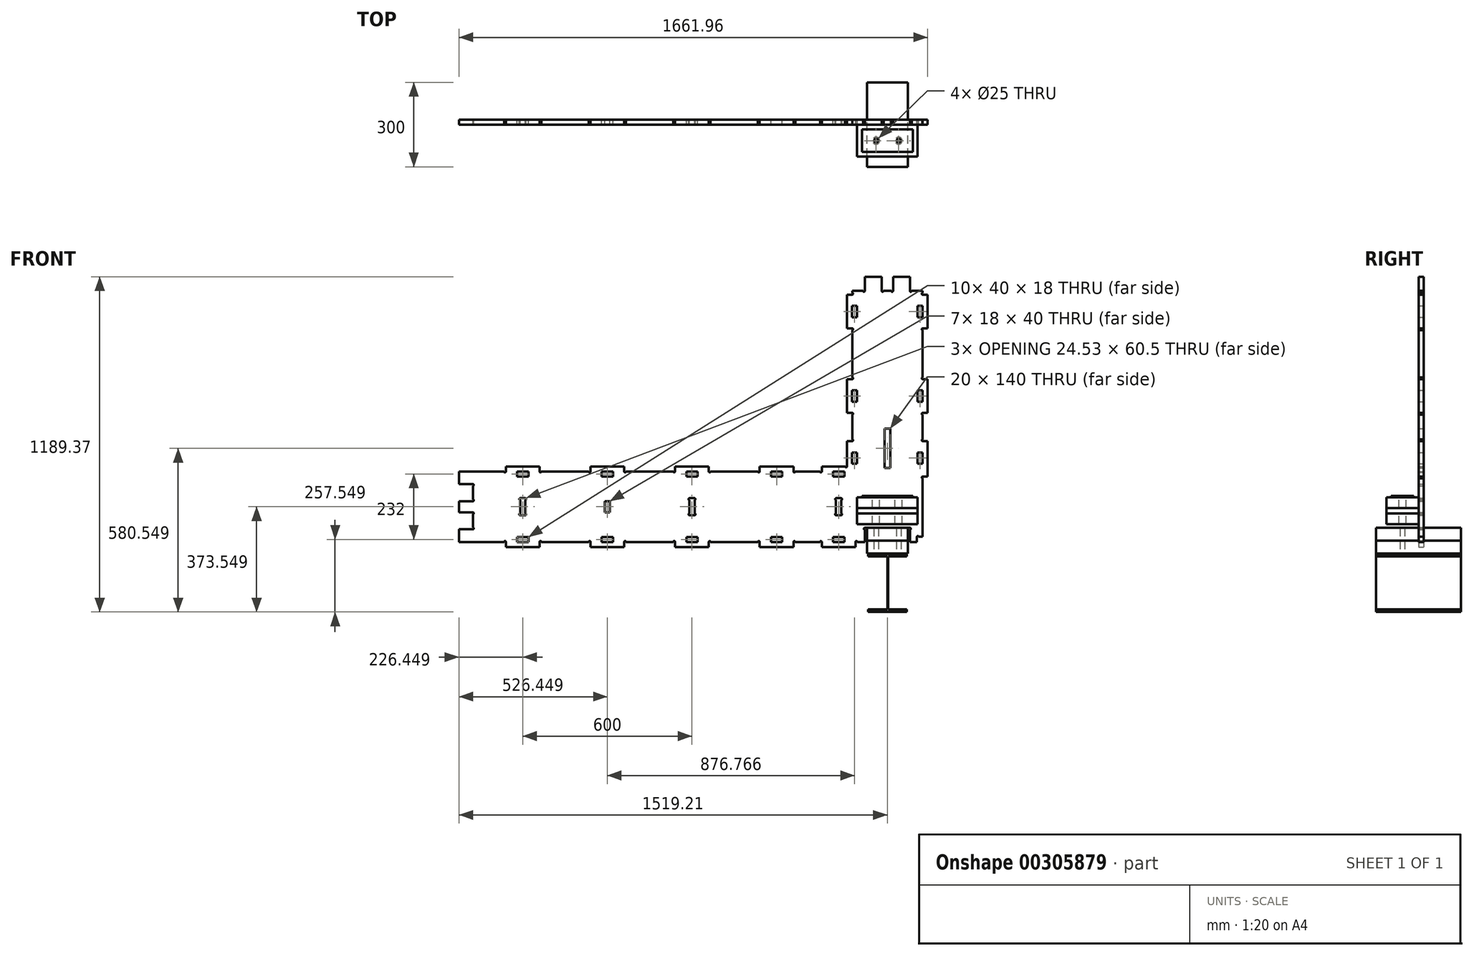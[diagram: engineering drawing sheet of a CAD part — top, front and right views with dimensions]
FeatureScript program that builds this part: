
annotation { "Feature Type Name" : "Feature", "Feature Type Description" : "" }
export const myFeature = defineFeature(function(context is Context, id is Id, definition is map)
    precondition{}
    {
        {
            var Q0;
            Q0=qCreatedBy(makeId("Front.planeOp"),FACE);
            var sketch = newSketch(context, id + "F0", { "sketchPlane" : qUnion([Q0])});
            skLineSegment(sketch, "E0", {"start": v(-425.29, 46.29) * mm, "end": v(-443.04, 46.29) * mm});
            skArc(sketch, "E1", {"start": v(-443.04, 46.29) * mm, "mid": v(-446.3, 49.43) * mm, "end": v(-443.29, 52.8) * mm});
            skLineSegment(sketch, "E2", {"start": v(-443.29, 52.8) * mm, "end": v(-443.29, 59.6) * mm});
            skLineSegment(sketch, "E3", {"start": v(-443.29, 59.6) * mm, "end": v(-481.77, 59.6) * mm});
            skArc(sketch, "E4", {"start": v(-481.77, 59.6) * mm, "mid": v(-485.15, 56.57) * mm, "end": v(-488.29, 59.84) * mm});
            skLineSegment(sketch, "E5", {"start": v(-488.29, 59.84) * mm, "end": v(-488.29, 109.6) * mm});
            skLineSegment(sketch, "E6", {"start": v(-488.29, 109.6) * mm, "end": v(-547.79, 109.6) * mm});
            skLineSegment(sketch, "E7", {"start": v(-547.79, 109.6) * mm, "end": v(-547.79, 59.84) * mm});
            skArc(sketch, "E8", {"start": v(-547.79, 59.84) * mm, "mid": v(-550.93, 56.58) * mm, "end": v(-554.3, 59.6) * mm});
            skLineSegment(sketch, "E9", {"start": v(-554.3, 59.6) * mm, "end": v(-581.77, 59.6) * mm});
            skArc(sketch, "E10", {"start": v(-581.77, 59.6) * mm, "mid": v(-585.15, 56.57) * mm, "end": v(-588.29, 59.84) * mm});
            skLineSegment(sketch, "E11", {"start": v(-588.29, 59.84) * mm, "end": v(-588.29, 109.6) * mm});
            skLineSegment(sketch, "E12", {"start": v(-588.29, 109.6) * mm, "end": v(-647.79, 109.6) * mm});
            skLineSegment(sketch, "E13", {"start": v(-647.79, 109.6) * mm, "end": v(-647.79, 59.84) * mm});
            skArc(sketch, "E14", {"start": v(-647.79, 59.84) * mm, "mid": v(-650.93, 56.58) * mm, "end": v(-654.3, 59.6) * mm});
            skLineSegment(sketch, "E15", {"start": v(-654.3, 59.6) * mm, "end": v(-692.79, 59.6) * mm});
            skLineSegment(sketch, "E16", {"start": v(-692.79, 59.6) * mm, "end": v(-692.79, 52.8) * mm});
            skArc(sketch, "E17", {"start": v(-692.79, 52.8) * mm, "mid": v(-689.77, 49.43) * mm, "end": v(-693.04, 46.29) * mm});
            skLineSegment(sketch, "E18", {"start": v(-693.04, 46.29) * mm, "end": v(-710.79, 46.29) * mm});
            skLineSegment(sketch, "E19", {"start": v(-710.79, 46.29) * mm, "end": v(-710.79, -73.21) * mm});
            skLineSegment(sketch, "E20", {"start": v(-710.79, -73.21) * mm, "end": v(-693.04, -73.21) * mm});
            skArc(sketch, "E21", {"start": v(-693.04, -73.21) * mm, "mid": v(-689.78, -76.35) * mm, "end": v(-692.79, -79.73) * mm});
            skLineSegment(sketch, "E22", {"start": v(-692.79, -79.73) * mm, "end": v(-692.79, -247.2) * mm});
            skArc(sketch, "E23", {"start": v(-692.79, -247.2) * mm, "mid": v(-689.77, -250.57) * mm, "end": v(-693.04, -253.71) * mm});
            skLineSegment(sketch, "E24", {"start": v(-693.04, -253.71) * mm, "end": v(-710.79, -253.71) * mm});
            skLineSegment(sketch, "E25", {"start": v(-710.79, -253.71) * mm, "end": v(-710.79, -373.21) * mm});
            skLineSegment(sketch, "E26", {"start": v(-710.79, -373.21) * mm, "end": v(-693.04, -373.21) * mm});
            skArc(sketch, "E27", {"start": v(-693.04, -373.21) * mm, "mid": v(-689.78, -376.35) * mm, "end": v(-692.79, -379.73) * mm});
            skLineSegment(sketch, "E28", {"start": v(-692.79, -379.73) * mm, "end": v(-692.79, -467.2) * mm});
            skArc(sketch, "E29", {"start": v(-692.79, -467.2) * mm, "mid": v(-689.77, -470.57) * mm, "end": v(-693.04, -473.71) * mm});
            skLineSegment(sketch, "E30", {"start": v(-693.04, -473.71) * mm, "end": v(-710.79, -473.71) * mm});
            skLineSegment(sketch, "E31", {"start": v(-710.79, -473.71) * mm, "end": v(-710.79, -563.23) * mm});
            skArc(sketch, "E32", {"start": v(-710.79, -563.23) * mm, "mid": v(-713.93, -566.49) * mm, "end": v(-717.3, -563.48) * mm});
            skLineSegment(sketch, "E33", {"start": v(-717.3, -563.48) * mm, "end": v(-800.55, -563.48) * mm});
            skLineSegment(sketch, "E34", {"start": v(-800.55, -563.48) * mm, "end": v(-800.55, -581.23) * mm});
            skArc(sketch, "E35", {"start": v(-800.55, -581.23) * mm, "mid": v(-803.7, -584.49) * mm, "end": v(-807.07, -581.48) * mm});
            skLineSegment(sketch, "E36", {"start": v(-807.07, -581.48) * mm, "end": v(-894.53, -581.48) * mm});
            skArc(sketch, "E37", {"start": v(-894.53, -581.48) * mm, "mid": v(-897.91, -584.5) * mm, "end": v(-901.05, -581.23) * mm});
            skLineSegment(sketch, "E38", {"start": v(-901.05, -581.23) * mm, "end": v(-901.05, -563.48) * mm});
            skLineSegment(sketch, "E39", {"start": v(-901.05, -563.48) * mm, "end": v(-1020.55, -563.48) * mm});
            skLineSegment(sketch, "E40", {"start": v(-1020.55, -563.48) * mm, "end": v(-1020.55, -581.23) * mm});
            skArc(sketch, "E41", {"start": v(-1020.55, -581.23) * mm, "mid": v(-1023.7, -584.49) * mm, "end": v(-1027.07, -581.48) * mm});
            skLineSegment(sketch, "E42", {"start": v(-1027.07, -581.48) * mm, "end": v(-1194.53, -581.48) * mm});
            skArc(sketch, "E43", {"start": v(-1194.53, -581.48) * mm, "mid": v(-1197.91, -584.5) * mm, "end": v(-1201.05, -581.23) * mm});
            skLineSegment(sketch, "E44", {"start": v(-1201.05, -581.23) * mm, "end": v(-1201.05, -563.48) * mm});
            skLineSegment(sketch, "E45", {"start": v(-1201.05, -563.48) * mm, "end": v(-1320.55, -563.48) * mm});
            skLineSegment(sketch, "E46", {"start": v(-1320.55, -563.48) * mm, "end": v(-1320.55, -581.23) * mm});
            skArc(sketch, "E47", {"start": v(-1320.55, -581.23) * mm, "mid": v(-1323.7, -584.49) * mm, "end": v(-1327.07, -581.48) * mm});
            skLineSegment(sketch, "E48", {"start": v(-1327.07, -581.48) * mm, "end": v(-1494.53, -581.48) * mm});
            skArc(sketch, "E49", {"start": v(-1494.53, -581.48) * mm, "mid": v(-1497.91, -584.5) * mm, "end": v(-1501.05, -581.23) * mm});
            skLineSegment(sketch, "E50", {"start": v(-1501.05, -581.23) * mm, "end": v(-1501.05, -563.48) * mm});
            skLineSegment(sketch, "E51", {"start": v(-1501.05, -563.48) * mm, "end": v(-1620.55, -563.48) * mm});
            skLineSegment(sketch, "E52", {"start": v(-1620.55, -563.48) * mm, "end": v(-1620.55, -581.23) * mm});
            skArc(sketch, "E53", {"start": v(-1620.55, -581.23) * mm, "mid": v(-1623.7, -584.49) * mm, "end": v(-1627.07, -581.48) * mm});
            skLineSegment(sketch, "E54", {"start": v(-1627.07, -581.48) * mm, "end": v(-1794.53, -581.48) * mm});
            skArc(sketch, "E55", {"start": v(-1794.53, -581.48) * mm, "mid": v(-1797.91, -584.5) * mm, "end": v(-1801.05, -581.23) * mm});
            skLineSegment(sketch, "E56", {"start": v(-1801.05, -581.23) * mm, "end": v(-1801.05, -563.48) * mm});
            skLineSegment(sketch, "E57", {"start": v(-1801.05, -563.48) * mm, "end": v(-1920.55, -563.48) * mm});
            skLineSegment(sketch, "E58", {"start": v(-1920.55, -563.48) * mm, "end": v(-1920.55, -581.23) * mm});
            skArc(sketch, "E59", {"start": v(-1920.55, -581.23) * mm, "mid": v(-1923.7, -584.49) * mm, "end": v(-1927.07, -581.48) * mm});
            skLineSegment(sketch, "E60", {"start": v(-1927.07, -581.48) * mm, "end": v(-2087.25, -581.48) * mm});
            skLineSegment(sketch, "E61", {"start": v(-2087.25, -581.48) * mm, "end": v(-2087.25, -625.98) * mm});
            skLineSegment(sketch, "E62", {"start": v(-2087.25, -625.98) * mm, "end": v(-2037.5, -625.98) * mm});
            skArc(sketch, "E63", {"start": v(-2037.5, -625.98) * mm, "mid": v(-2034.24, -629.12) * mm, "end": v(-2037.25, -632.5) * mm});
            skLineSegment(sketch, "E64", {"start": v(-2037.25, -632.5) * mm, "end": v(-2037.25, -679.96) * mm});
            skArc(sketch, "E65", {"start": v(-2037.25, -679.96) * mm, "mid": v(-2034.23, -683.34) * mm, "end": v(-2037.5, -686.48) * mm});
            skLineSegment(sketch, "E66", {"start": v(-2037.5, -686.48) * mm, "end": v(-2087.25, -686.48) * mm});
            skLineSegment(sketch, "E67", {"start": v(-2087.25, -686.48) * mm, "end": v(-2087.25, -725.98) * mm});
            skLineSegment(sketch, "E68", {"start": v(-2087.25, -725.98) * mm, "end": v(-2037.5, -725.98) * mm});
            skArc(sketch, "E69", {"start": v(-2037.5, -725.98) * mm, "mid": v(-2034.24, -729.12) * mm, "end": v(-2037.25, -732.5) * mm});
            skLineSegment(sketch, "E70", {"start": v(-2037.25, -732.5) * mm, "end": v(-2037.25, -779.96) * mm});
            skArc(sketch, "E71", {"start": v(-2037.25, -779.96) * mm, "mid": v(-2034.23, -783.34) * mm, "end": v(-2037.5, -786.48) * mm});
            skLineSegment(sketch, "E72", {"start": v(-2037.5, -786.48) * mm, "end": v(-2087.25, -786.48) * mm});
            skLineSegment(sketch, "E73", {"start": v(-2087.25, -786.48) * mm, "end": v(-2087.25, -830.98) * mm});
            skLineSegment(sketch, "E74", {"start": v(-2087.25, -830.98) * mm, "end": v(-1927.07, -830.98) * mm});
            skArc(sketch, "E75", {"start": v(-1927.07, -830.98) * mm, "mid": v(-1923.7, -827.96) * mm, "end": v(-1920.55, -831.23) * mm});
            skLineSegment(sketch, "E76", {"start": v(-1920.55, -831.23) * mm, "end": v(-1920.55, -848.98) * mm});
            skLineSegment(sketch, "E77", {"start": v(-1920.55, -848.98) * mm, "end": v(-1801.05, -848.98) * mm});
            skLineSegment(sketch, "E78", {"start": v(-1801.05, -848.98) * mm, "end": v(-1801.05, -831.23) * mm});
            skArc(sketch, "E79", {"start": v(-1801.05, -831.23) * mm, "mid": v(-1797.91, -827.97) * mm, "end": v(-1794.53, -830.98) * mm});
            skLineSegment(sketch, "E80", {"start": v(-1794.53, -830.98) * mm, "end": v(-1627.07, -830.98) * mm});
            skArc(sketch, "E81", {"start": v(-1627.07, -830.98) * mm, "mid": v(-1623.7, -827.96) * mm, "end": v(-1620.55, -831.23) * mm});
            skLineSegment(sketch, "E82", {"start": v(-1620.55, -831.23) * mm, "end": v(-1620.55, -848.98) * mm});
            skLineSegment(sketch, "E83", {"start": v(-1620.55, -848.98) * mm, "end": v(-1501.05, -848.98) * mm});
            skLineSegment(sketch, "E84", {"start": v(-1501.05, -848.98) * mm, "end": v(-1501.05, -831.23) * mm});
            skArc(sketch, "E85", {"start": v(-1501.05, -831.23) * mm, "mid": v(-1497.91, -827.97) * mm, "end": v(-1494.53, -830.98) * mm});
            skLineSegment(sketch, "E86", {"start": v(-1494.53, -830.98) * mm, "end": v(-1327.07, -830.98) * mm});
            skArc(sketch, "E87", {"start": v(-1327.07, -830.98) * mm, "mid": v(-1323.7, -827.96) * mm, "end": v(-1320.55, -831.23) * mm});
            skLineSegment(sketch, "E88", {"start": v(-1320.55, -831.23) * mm, "end": v(-1320.55, -848.98) * mm});
            skLineSegment(sketch, "E89", {"start": v(-1320.55, -848.98) * mm, "end": v(-1201.05, -848.98) * mm});
            skLineSegment(sketch, "E90", {"start": v(-1201.05, -848.98) * mm, "end": v(-1201.05, -831.23) * mm});
            skArc(sketch, "E91", {"start": v(-1201.05, -831.23) * mm, "mid": v(-1197.91, -827.97) * mm, "end": v(-1194.53, -830.98) * mm});
            skLineSegment(sketch, "E92", {"start": v(-1194.53, -830.98) * mm, "end": v(-1027.07, -830.98) * mm});
            skArc(sketch, "E93", {"start": v(-1027.07, -830.98) * mm, "mid": v(-1023.7, -827.96) * mm, "end": v(-1020.55, -831.23) * mm});
            skLineSegment(sketch, "E94", {"start": v(-1020.55, -831.23) * mm, "end": v(-1020.55, -848.98) * mm});
            skLineSegment(sketch, "E95", {"start": v(-1020.55, -848.98) * mm, "end": v(-901.05, -848.98) * mm});
            skLineSegment(sketch, "E96", {"start": v(-901.05, -848.98) * mm, "end": v(-901.05, -831.23) * mm});
            skArc(sketch, "E97", {"start": v(-901.05, -831.23) * mm, "mid": v(-897.91, -827.97) * mm, "end": v(-894.53, -830.98) * mm});
            skLineSegment(sketch, "E98", {"start": v(-894.53, -830.98) * mm, "end": v(-807.07, -830.98) * mm});
            skArc(sketch, "E99", {"start": v(-807.07, -830.98) * mm, "mid": v(-803.7, -827.96) * mm, "end": v(-800.55, -831.23) * mm});
            skLineSegment(sketch, "E100", {"start": v(-800.55, -831.23) * mm, "end": v(-800.55, -848.98) * mm});
            skLineSegment(sketch, "E101", {"start": v(-800.55, -848.98) * mm, "end": v(-681.05, -848.98) * mm});
            skLineSegment(sketch, "E102", {"start": v(-681.05, -848.98) * mm, "end": v(-681.05, -831.23) * mm});
            skArc(sketch, "E103", {"start": v(-681.05, -831.23) * mm, "mid": v(-677.91, -827.97) * mm, "end": v(-674.53, -830.98) * mm});
            skLineSegment(sketch, "E104", {"start": v(-674.53, -830.98) * mm, "end": v(-648.29, -830.98) * mm});
            skLineSegment(sketch, "E105", {"start": v(-648.29, -830.98) * mm, "end": v(-648.29, -787.5) * mm});
            skArc(sketch, "E106", {"start": v(-648.29, -787.5) * mm, "mid": v(-651.3, -784.12) * mm, "end": v(-648.04, -780.98) * mm});
            skLineSegment(sketch, "E107", {"start": v(-648.04, -780.98) * mm, "end": v(-488.04, -780.98) * mm});
            skArc(sketch, "E108", {"start": v(-488.04, -780.98) * mm, "mid": v(-484.78, -784.12) * mm, "end": v(-487.79, -787.5) * mm});
            skLineSegment(sketch, "E109", {"start": v(-487.79, -787.5) * mm, "end": v(-487.79, -830.98) * mm});
            skLineSegment(sketch, "E110", {"start": v(-487.79, -830.98) * mm, "end": v(-463.29, -830.98) * mm});
            skLineSegment(sketch, "E111", {"start": v(-463.29, -830.98) * mm, "end": v(-463.29, -813.23) * mm});
            skArc(sketch, "E112", {"start": v(-463.29, -813.23) * mm, "mid": v(-460.15, -809.97) * mm, "end": v(-456.77, -812.98) * mm});
            skLineSegment(sketch, "E113", {"start": v(-456.77, -812.98) * mm, "end": v(-443.29, -812.98) * mm});
            skLineSegment(sketch, "E114", {"start": v(-443.29, -812.98) * mm, "end": v(-443.29, -605.5) * mm});
            skArc(sketch, "E115", {"start": v(-443.29, -605.5) * mm, "mid": v(-446.3, -602.12) * mm, "end": v(-443.04, -598.99) * mm});
            skLineSegment(sketch, "E116", {"start": v(-443.04, -598.99) * mm, "end": v(-425.29, -598.99) * mm});
            skLineSegment(sketch, "E117", {"start": v(-425.29, -598.99) * mm, "end": v(-425.29, -473.71) * mm});
            skLineSegment(sketch, "E118", {"start": v(-425.29, -473.71) * mm, "end": v(-443.04, -473.71) * mm});
            skArc(sketch, "E119", {"start": v(-443.04, -473.71) * mm, "mid": v(-446.3, -470.57) * mm, "end": v(-443.29, -467.2) * mm});
            skLineSegment(sketch, "E120", {"start": v(-443.29, -467.2) * mm, "end": v(-443.29, -379.73) * mm});
            skArc(sketch, "E121", {"start": v(-443.29, -379.73) * mm, "mid": v(-446.3, -376.35) * mm, "end": v(-443.04, -373.21) * mm});
            skLineSegment(sketch, "E122", {"start": v(-443.04, -373.21) * mm, "end": v(-425.29, -373.21) * mm});
            skLineSegment(sketch, "E123", {"start": v(-425.29, -373.21) * mm, "end": v(-425.29, -253.71) * mm});
            skLineSegment(sketch, "E124", {"start": v(-425.29, -253.71) * mm, "end": v(-443.04, -253.71) * mm});
            skArc(sketch, "E125", {"start": v(-443.04, -253.71) * mm, "mid": v(-446.3, -250.57) * mm, "end": v(-443.29, -247.2) * mm});
            skLineSegment(sketch, "E126", {"start": v(-443.29, -247.2) * mm, "end": v(-443.29, -79.73) * mm});
            skArc(sketch, "E127", {"start": v(-443.29, -79.73) * mm, "mid": v(-446.3, -76.35) * mm, "end": v(-443.04, -73.21) * mm});
            skLineSegment(sketch, "E128", {"start": v(-443.04, -73.21) * mm, "end": v(-425.29, -73.21) * mm});
            skLineSegment(sketch, "E129", {"start": v(-425.29, -73.21) * mm, "end": v(-425.29, 46.29) * mm});
            skLineSegment(sketch, "E130", {"start": v(-1840.8, -813.23) * mm, "end": v(-1880.8, -813.23) * mm});
            skLineSegment(sketch, "E131", {"start": v(-1880.8, -813.23) * mm, "end": v(-1880.8, -831.23) * mm});
            skLineSegment(sketch, "E132", {"start": v(-1880.8, -831.23) * mm, "end": v(-1840.8, -831.23) * mm});
            skLineSegment(sketch, "E133", {"start": v(-1840.8, -831.23) * mm, "end": v(-1840.8, -813.23) * mm});
            skArc(sketch, "E134", {"start": v(-1869.8, -675.98) * mm, "mid": v(-1873.07, -679.12) * mm, "end": v(-1870.05, -682.5) * mm});
            skLineSegment(sketch, "E135", {"start": v(-1870.05, -682.5) * mm, "end": v(-1870.05, -729.96) * mm});
            skArc(sketch, "E136", {"start": v(-1870.05, -729.96) * mm, "mid": v(-1873.06, -733.34) * mm, "end": v(-1869.8, -736.48) * mm});
            skLineSegment(sketch, "E137", {"start": v(-1869.8, -736.48) * mm, "end": v(-1851.8, -736.48) * mm});
            skArc(sketch, "E138", {"start": v(-1851.8, -736.48) * mm, "mid": v(-1848.54, -733.34) * mm, "end": v(-1851.55, -729.96) * mm});
            skLineSegment(sketch, "E139", {"start": v(-1851.55, -729.96) * mm, "end": v(-1851.55, -682.5) * mm});
            skArc(sketch, "E140", {"start": v(-1851.55, -682.5) * mm, "mid": v(-1848.54, -679.12) * mm, "end": v(-1851.8, -675.98) * mm});
            skLineSegment(sketch, "E141", {"start": v(-1851.8, -675.98) * mm, "end": v(-1869.8, -675.98) * mm});
            skLineSegment(sketch, "E142", {"start": v(-1840.8, -599.23) * mm, "end": v(-1840.8, -581.23) * mm});
            skLineSegment(sketch, "E143", {"start": v(-1840.8, -581.23) * mm, "end": v(-1880.8, -581.23) * mm});
            skLineSegment(sketch, "E144", {"start": v(-1880.8, -581.23) * mm, "end": v(-1880.8, -599.23) * mm});
            skLineSegment(sketch, "E145", {"start": v(-1880.8, -599.23) * mm, "end": v(-1840.8, -599.23) * mm});
            skLineSegment(sketch, "E146", {"start": v(-1580.8, -813.23) * mm, "end": v(-1580.8, -831.23) * mm});
            skLineSegment(sketch, "E147", {"start": v(-1580.8, -831.23) * mm, "end": v(-1540.8, -831.23) * mm});
            skLineSegment(sketch, "E148", {"start": v(-1540.8, -831.23) * mm, "end": v(-1540.8, -813.23) * mm});
            skLineSegment(sketch, "E149", {"start": v(-1540.8, -813.23) * mm, "end": v(-1580.8, -813.23) * mm});
            skLineSegment(sketch, "E150", {"start": v(-1569.8, -686.23) * mm, "end": v(-1569.8, -726.23) * mm});
            skLineSegment(sketch, "E151", {"start": v(-1569.8, -726.23) * mm, "end": v(-1551.8, -726.23) * mm});
            skLineSegment(sketch, "E152", {"start": v(-1551.8, -726.23) * mm, "end": v(-1551.8, -686.23) * mm});
            skLineSegment(sketch, "E153", {"start": v(-1551.8, -686.23) * mm, "end": v(-1569.8, -686.23) * mm});
            skLineSegment(sketch, "E154", {"start": v(-1580.8, -599.23) * mm, "end": v(-1540.8, -599.23) * mm});
            skLineSegment(sketch, "E155", {"start": v(-1540.8, -599.23) * mm, "end": v(-1540.8, -581.23) * mm});
            skLineSegment(sketch, "E156", {"start": v(-1540.8, -581.23) * mm, "end": v(-1580.8, -581.23) * mm});
            skLineSegment(sketch, "E157", {"start": v(-1580.8, -581.23) * mm, "end": v(-1580.8, -599.23) * mm});
            skLineSegment(sketch, "E158", {"start": v(-1280.8, -813.23) * mm, "end": v(-1280.8, -831.23) * mm});
            skLineSegment(sketch, "E159", {"start": v(-1280.8, -831.23) * mm, "end": v(-1240.8, -831.23) * mm});
            skLineSegment(sketch, "E160", {"start": v(-1240.8, -831.23) * mm, "end": v(-1240.8, -813.23) * mm});
            skLineSegment(sketch, "E161", {"start": v(-1240.8, -813.23) * mm, "end": v(-1280.8, -813.23) * mm});
            skArc(sketch, "E162", {"start": v(-1269.8, -675.98) * mm, "mid": v(-1273.07, -679.12) * mm, "end": v(-1270.05, -682.5) * mm});
            skLineSegment(sketch, "E163", {"start": v(-1270.05, -682.5) * mm, "end": v(-1270.05, -729.96) * mm});
            skArc(sketch, "E164", {"start": v(-1270.05, -729.96) * mm, "mid": v(-1273.06, -733.34) * mm, "end": v(-1269.8, -736.48) * mm});
            skLineSegment(sketch, "E165", {"start": v(-1269.8, -736.48) * mm, "end": v(-1251.8, -736.48) * mm});
            skArc(sketch, "E166", {"start": v(-1251.8, -736.48) * mm, "mid": v(-1248.54, -733.34) * mm, "end": v(-1251.55, -729.96) * mm});
            skLineSegment(sketch, "E167", {"start": v(-1251.55, -729.96) * mm, "end": v(-1251.55, -682.5) * mm});
            skArc(sketch, "E168", {"start": v(-1251.55, -682.5) * mm, "mid": v(-1248.54, -679.12) * mm, "end": v(-1251.8, -675.98) * mm});
            skLineSegment(sketch, "E169", {"start": v(-1251.8, -675.98) * mm, "end": v(-1269.8, -675.98) * mm});
            skLineSegment(sketch, "E170", {"start": v(-1280.8, -599.23) * mm, "end": v(-1240.8, -599.23) * mm});
            skLineSegment(sketch, "E171", {"start": v(-1240.8, -599.23) * mm, "end": v(-1240.8, -581.23) * mm});
            skLineSegment(sketch, "E172", {"start": v(-1240.8, -581.23) * mm, "end": v(-1280.8, -581.23) * mm});
            skLineSegment(sketch, "E173", {"start": v(-1280.8, -581.23) * mm, "end": v(-1280.8, -599.23) * mm});
            skLineSegment(sketch, "E174", {"start": v(-980.8, -813.23) * mm, "end": v(-980.8, -831.23) * mm});
            skLineSegment(sketch, "E175", {"start": v(-980.8, -831.23) * mm, "end": v(-940.8, -831.23) * mm});
            skLineSegment(sketch, "E176", {"start": v(-940.8, -831.23) * mm, "end": v(-940.8, -813.23) * mm});
            skLineSegment(sketch, "E177", {"start": v(-940.8, -813.23) * mm, "end": v(-980.8, -813.23) * mm});
            skLineSegment(sketch, "E178", {"start": v(-980.8, -599.23) * mm, "end": v(-940.8, -599.23) * mm});
            skLineSegment(sketch, "E179", {"start": v(-940.8, -599.23) * mm, "end": v(-940.8, -581.23) * mm});
            skLineSegment(sketch, "E180", {"start": v(-940.8, -581.23) * mm, "end": v(-980.8, -581.23) * mm});
            skLineSegment(sketch, "E181", {"start": v(-980.8, -581.23) * mm, "end": v(-980.8, -599.23) * mm});
            skLineSegment(sketch, "E182", {"start": v(-760.8, -813.23) * mm, "end": v(-760.8, -831.23) * mm});
            skLineSegment(sketch, "E183", {"start": v(-760.8, -831.23) * mm, "end": v(-720.8, -831.23) * mm});
            skLineSegment(sketch, "E184", {"start": v(-720.8, -831.23) * mm, "end": v(-720.8, -813.23) * mm});
            skLineSegment(sketch, "E185", {"start": v(-720.8, -813.23) * mm, "end": v(-760.8, -813.23) * mm});
            skArc(sketch, "E186", {"start": v(-749.8, -675.98) * mm, "mid": v(-753.07, -679.12) * mm, "end": v(-750.05, -682.5) * mm});
            skLineSegment(sketch, "E187", {"start": v(-750.05, -682.5) * mm, "end": v(-750.05, -729.96) * mm});
            skArc(sketch, "E188", {"start": v(-750.05, -729.96) * mm, "mid": v(-753.06, -733.34) * mm, "end": v(-749.8, -736.48) * mm});
            skLineSegment(sketch, "E189", {"start": v(-749.8, -736.48) * mm, "end": v(-731.8, -736.48) * mm});
            skArc(sketch, "E190", {"start": v(-731.8, -736.48) * mm, "mid": v(-728.54, -733.34) * mm, "end": v(-731.55, -729.96) * mm});
            skLineSegment(sketch, "E191", {"start": v(-731.55, -729.96) * mm, "end": v(-731.55, -682.5) * mm});
            skArc(sketch, "E192", {"start": v(-731.55, -682.5) * mm, "mid": v(-728.54, -679.12) * mm, "end": v(-731.8, -675.98) * mm});
            skLineSegment(sketch, "E193", {"start": v(-731.8, -675.98) * mm, "end": v(-749.8, -675.98) * mm});
            skLineSegment(sketch, "E194", {"start": v(-760.8, -599.23) * mm, "end": v(-720.8, -599.23) * mm});
            skLineSegment(sketch, "E195", {"start": v(-720.8, -599.23) * mm, "end": v(-720.8, -581.23) * mm});
            skLineSegment(sketch, "E196", {"start": v(-720.8, -581.23) * mm, "end": v(-760.8, -581.23) * mm});
            skLineSegment(sketch, "E197", {"start": v(-760.8, -581.23) * mm, "end": v(-760.8, -599.23) * mm});
            skLineSegment(sketch, "E198", {"start": v(-693.04, -553.46) * mm, "end": v(-675.04, -553.46) * mm});
            skLineSegment(sketch, "E199", {"start": v(-675.04, -553.46) * mm, "end": v(-675.04, -513.46) * mm});
            skLineSegment(sketch, "E200", {"start": v(-675.04, -513.46) * mm, "end": v(-693.04, -513.46) * mm});
            skLineSegment(sketch, "E201", {"start": v(-693.04, -513.46) * mm, "end": v(-693.04, -553.46) * mm});
            skArc(sketch, "E202", {"start": v(-608.29, -606.19) * mm, "mid": v(-605.15, -609.45) * mm, "end": v(-601.77, -606.44) * mm});
            skLineSegment(sketch, "E203", {"start": v(-601.77, -599.48) * mm, "end": v(-534.3, -599.48) * mm});
            skArc(sketch, "E204", {"start": v(-534.3, -599.48) * mm, "mid": v(-530.92, -602.49) * mm, "end": v(-527.79, -599.23) * mm});
            skLineSegment(sketch, "E205", {"start": v(-527.79, -599.23) * mm, "end": v(-527.79, -581.23) * mm});
            skArc(sketch, "E206", {"start": v(-527.79, -581.23) * mm, "mid": v(-530.92, -577.97) * mm, "end": v(-534.3, -580.98) * mm});
            skLineSegment(sketch, "E207", {"start": v(-534.3, -580.98) * mm, "end": v(-601.77, -580.98) * mm});
            skArc(sketch, "E208", {"start": v(-601.77, -580.98) * mm, "mid": v(-605.15, -577.97) * mm, "end": v(-608.29, -581.23) * mm});
            skLineSegment(sketch, "E209", {"start": v(-608.29, -581.23) * mm, "end": v(-608.29, -599.23) * mm});
            skLineSegment(sketch, "E210", {"start": v(-558.04, -569.23) * mm, "end": v(-558.04, -429.23) * mm});
            skLineSegment(sketch, "E211", {"start": v(-558.04, -429.23) * mm, "end": v(-578.04, -429.23) * mm});
            skLineSegment(sketch, "E212", {"start": v(-578.04, -429.23) * mm, "end": v(-578.04, -569.23) * mm});
            skLineSegment(sketch, "E213", {"start": v(-578.04, -569.23) * mm, "end": v(-558.04, -569.23) * mm});
            skLineSegment(sketch, "E214", {"start": v(-461.04, -553.46) * mm, "end": v(-443.04, -553.46) * mm});
            skLineSegment(sketch, "E215", {"start": v(-443.04, -553.46) * mm, "end": v(-443.04, -513.46) * mm});
            skLineSegment(sketch, "E216", {"start": v(-443.04, -513.46) * mm, "end": v(-461.04, -513.46) * mm});
            skLineSegment(sketch, "E217", {"start": v(-461.04, -513.46) * mm, "end": v(-461.04, -553.46) * mm});
            skLineSegment(sketch, "E218", {"start": v(-461.04, -333.46) * mm, "end": v(-443.04, -333.46) * mm});
            skLineSegment(sketch, "E219", {"start": v(-443.04, -333.46) * mm, "end": v(-443.04, -293.46) * mm});
            skLineSegment(sketch, "E220", {"start": v(-443.04, -293.46) * mm, "end": v(-461.04, -293.46) * mm});
            skLineSegment(sketch, "E221", {"start": v(-461.04, -293.46) * mm, "end": v(-461.04, -333.46) * mm});
            skLineSegment(sketch, "E222", {"start": v(-693.04, -333.46) * mm, "end": v(-675.04, -333.46) * mm});
            skLineSegment(sketch, "E223", {"start": v(-675.04, -333.46) * mm, "end": v(-675.04, -293.46) * mm});
            skLineSegment(sketch, "E224", {"start": v(-675.04, -293.46) * mm, "end": v(-693.04, -293.46) * mm});
            skLineSegment(sketch, "E225", {"start": v(-693.04, -293.46) * mm, "end": v(-693.04, -333.46) * mm});
            skLineSegment(sketch, "E226", {"start": v(-693.04, -33.46) * mm, "end": v(-675.04, -33.46) * mm});
            skLineSegment(sketch, "E227", {"start": v(-675.04, -33.46) * mm, "end": v(-675.04, 6.54) * mm});
            skLineSegment(sketch, "E228", {"start": v(-675.04, 6.54) * mm, "end": v(-693.04, 6.54) * mm});
            skLineSegment(sketch, "E229", {"start": v(-693.04, 6.54) * mm, "end": v(-693.04, -33.46) * mm});
            skLineSegment(sketch, "E230", {"start": v(-461.04, -33.46) * mm, "end": v(-443.04, -33.46) * mm});
            skLineSegment(sketch, "E231", {"start": v(-443.04, -33.46) * mm, "end": v(-443.04, 6.54) * mm});
            skLineSegment(sketch, "E232", {"start": v(-443.04, 6.54) * mm, "end": v(-461.04, 6.54) * mm});
            skLineSegment(sketch, "E233", {"start": v(-461.04, 6.54) * mm, "end": v(-461.04, -33.46) * mm});
            skLineSegment(sketch, "E234.bottom", {"start": v(-675.04, -553.46) * mm, "end": v(-461.04, -553.46) * mm, "construction": true});
            skLineSegment(sketch, "E234.top", {"start": v(-675.04, -801.54) * mm, "end": v(-461.04, -801.54) * mm, "construction": true});
            skLineSegment(sketch, "E234.left", {"start": v(-675.04, -553.46) * mm, "end": v(-675.04, -801.54) * mm, "construction": true});
            skLineSegment(sketch, "E234.right", {"start": v(-461.04, -553.46) * mm, "end": v(-461.04, -801.54) * mm, "construction": true});
            skLineSegment(sketch, "E235.bottom", {"start": v(-608.29, -606.19) * mm, "end": v(-527.4, -606.19) * mm, "construction": true});
            skLineSegment(sketch, "E235.top", {"start": v(-608.29, -686.19) * mm, "end": v(-527.4, -686.19) * mm, "construction": true});
            skLineSegment(sketch, "E235.left", {"start": v(-608.29, -606.19) * mm, "end": v(-608.29, -686.19) * mm, "construction": true});
            skLineSegment(sketch, "E235.right", {"start": v(-527.4, -606.19) * mm, "end": v(-527.4, -686.19) * mm, "construction": true});
            skSolve(sketch);
        }
        {
            var Q0;
            Q0 = qSketchRegion(id + "F0", true);
            extrude(context, id + "F1", {"entities" : qUnion([Q0]), "depth" : 18 * mm});
        }
        {
            var Q0;
            Q0=makeQuery(id+"F1.opExtrude","CAP_FACE",FACE,{"disambiguationData":[OSD([sQuery(id+"F0.wireOp",EDGE,"E0"),sQuery(id+"F0.wireOp",EDGE,"E1"),sQuery(id+"F0.wireOp",EDGE,"E2"),sQuery(id+"F0.wireOp",EDGE,"E3"),sQuery(id+"F0.wireOp",EDGE,"E4"),sQuery(id+"F0.wireOp",EDGE,"E5"),sQuery(id+"F0.wireOp",EDGE,"E6"),sQuery(id+"F0.wireOp",EDGE,"E7"),sQuery(id+"F0.wireOp",EDGE,"E8"),sQuery(id+"F0.wireOp",EDGE,"E9"),sQuery(id+"F0.wireOp",EDGE,"E10"),sQuery(id+"F0.wireOp",EDGE,"E11"),sQuery(id+"F0.wireOp",EDGE,"E12"),sQuery(id+"F0.wireOp",EDGE,"E13"),sQuery(id+"F0.wireOp",EDGE,"E14"),sQuery(id+"F0.wireOp",EDGE,"E15"),sQuery(id+"F0.wireOp",EDGE,"E16"),sQuery(id+"F0.wireOp",EDGE,"E17"),sQuery(id+"F0.wireOp",EDGE,"E18"),sQuery(id+"F0.wireOp",EDGE,"E19"),sQuery(id+"F0.wireOp",EDGE,"E20"),sQuery(id+"F0.wireOp",EDGE,"E21"),sQuery(id+"F0.wireOp",EDGE,"E22"),sQuery(id+"F0.wireOp",EDGE,"E23"),sQuery(id+"F0.wireOp",EDGE,"E24"),sQuery(id+"F0.wireOp",EDGE,"E25"),sQuery(id+"F0.wireOp",EDGE,"E26"),sQuery(id+"F0.wireOp",EDGE,"E27"),sQuery(id+"F0.wireOp",EDGE,"E28"),sQuery(id+"F0.wireOp",EDGE,"E29"),sQuery(id+"F0.wireOp",EDGE,"E30"),sQuery(id+"F0.wireOp",EDGE,"E31"),sQuery(id+"F0.wireOp",EDGE,"E32"),sQuery(id+"F0.wireOp",EDGE,"E33"),sQuery(id+"F0.wireOp",EDGE,"E34"),sQuery(id+"F0.wireOp",EDGE,"E35"),sQuery(id+"F0.wireOp",EDGE,"E36"),sQuery(id+"F0.wireOp",EDGE,"E37"),sQuery(id+"F0.wireOp",EDGE,"E38"),sQuery(id+"F0.wireOp",EDGE,"E39"),sQuery(id+"F0.wireOp",EDGE,"E40"),sQuery(id+"F0.wireOp",EDGE,"E41"),sQuery(id+"F0.wireOp",EDGE,"E42"),sQuery(id+"F0.wireOp",EDGE,"E43"),sQuery(id+"F0.wireOp",EDGE,"E44"),sQuery(id+"F0.wireOp",EDGE,"E45"),sQuery(id+"F0.wireOp",EDGE,"E46"),sQuery(id+"F0.wireOp",EDGE,"E47"),sQuery(id+"F0.wireOp",EDGE,"E48"),sQuery(id+"F0.wireOp",EDGE,"E49"),sQuery(id+"F0.wireOp",EDGE,"E50"),sQuery(id+"F0.wireOp",EDGE,"E51"),sQuery(id+"F0.wireOp",EDGE,"E52"),sQuery(id+"F0.wireOp",EDGE,"E53"),sQuery(id+"F0.wireOp",EDGE,"E54"),sQuery(id+"F0.wireOp",EDGE,"E55"),sQuery(id+"F0.wireOp",EDGE,"E56"),sQuery(id+"F0.wireOp",EDGE,"E57"),sQuery(id+"F0.wireOp",EDGE,"E58"),sQuery(id+"F0.wireOp",EDGE,"E59"),sQuery(id+"F0.wireOp",EDGE,"E60"),sQuery(id+"F0.wireOp",EDGE,"E61"),sQuery(id+"F0.wireOp",EDGE,"E62"),sQuery(id+"F0.wireOp",EDGE,"E63"),sQuery(id+"F0.wireOp",EDGE,"E64"),sQuery(id+"F0.wireOp",EDGE,"E65"),sQuery(id+"F0.wireOp",EDGE,"E66"),sQuery(id+"F0.wireOp",EDGE,"E67"),sQuery(id+"F0.wireOp",EDGE,"E68"),sQuery(id+"F0.wireOp",EDGE,"E69"),sQuery(id+"F0.wireOp",EDGE,"E70"),sQuery(id+"F0.wireOp",EDGE,"E71"),sQuery(id+"F0.wireOp",EDGE,"E72"),sQuery(id+"F0.wireOp",EDGE,"E73"),sQuery(id+"F0.wireOp",EDGE,"E74"),sQuery(id+"F0.wireOp",EDGE,"E75"),sQuery(id+"F0.wireOp",EDGE,"E76"),sQuery(id+"F0.wireOp",EDGE,"E77"),sQuery(id+"F0.wireOp",EDGE,"E78"),sQuery(id+"F0.wireOp",EDGE,"E79"),sQuery(id+"F0.wireOp",EDGE,"E80"),sQuery(id+"F0.wireOp",EDGE,"E81"),sQuery(id+"F0.wireOp",EDGE,"E82"),sQuery(id+"F0.wireOp",EDGE,"E83"),sQuery(id+"F0.wireOp",EDGE,"E84"),sQuery(id+"F0.wireOp",EDGE,"E85"),sQuery(id+"F0.wireOp",EDGE,"E86"),sQuery(id+"F0.wireOp",EDGE,"E87"),sQuery(id+"F0.wireOp",EDGE,"E88"),sQuery(id+"F0.wireOp",EDGE,"E89"),sQuery(id+"F0.wireOp",EDGE,"E90"),sQuery(id+"F0.wireOp",EDGE,"E91"),sQuery(id+"F0.wireOp",EDGE,"E92"),sQuery(id+"F0.wireOp",EDGE,"E93"),sQuery(id+"F0.wireOp",EDGE,"E94"),sQuery(id+"F0.wireOp",EDGE,"E95"),sQuery(id+"F0.wireOp",EDGE,"E96"),sQuery(id+"F0.wireOp",EDGE,"E97"),sQuery(id+"F0.wireOp",EDGE,"E98"),sQuery(id+"F0.wireOp",EDGE,"E99"),sQuery(id+"F0.wireOp",EDGE,"E100"),sQuery(id+"F0.wireOp",EDGE,"E101"),sQuery(id+"F0.wireOp",EDGE,"E102"),sQuery(id+"F0.wireOp",EDGE,"E103"),sQuery(id+"F0.wireOp",EDGE,"E104"),sQuery(id+"F0.wireOp",EDGE,"E105"),sQuery(id+"F0.wireOp",EDGE,"E106"),sQuery(id+"F0.wireOp",EDGE,"E107"),sQuery(id+"F0.wireOp",EDGE,"E108"),sQuery(id+"F0.wireOp",EDGE,"E109"),sQuery(id+"F0.wireOp",EDGE,"E110"),sQuery(id+"F0.wireOp",EDGE,"E111"),sQuery(id+"F0.wireOp",EDGE,"E112"),sQuery(id+"F0.wireOp",EDGE,"E113"),sQuery(id+"F0.wireOp",EDGE,"E114"),sQuery(id+"F0.wireOp",EDGE,"E115"),sQuery(id+"F0.wireOp",EDGE,"E116"),sQuery(id+"F0.wireOp",EDGE,"E117"),sQuery(id+"F0.wireOp",EDGE,"E118"),sQuery(id+"F0.wireOp",EDGE,"E119"),sQuery(id+"F0.wireOp",EDGE,"E120"),sQuery(id+"F0.wireOp",EDGE,"E121"),sQuery(id+"F0.wireOp",EDGE,"E122"),sQuery(id+"F0.wireOp",EDGE,"E123"),sQuery(id+"F0.wireOp",EDGE,"E124"),sQuery(id+"F0.wireOp",EDGE,"E125"),sQuery(id+"F0.wireOp",EDGE,"E126"),sQuery(id+"F0.wireOp",EDGE,"E127"),sQuery(id+"F0.wireOp",EDGE,"E128"),sQuery(id+"F0.wireOp",EDGE,"E129"),sQuery(id+"F0.wireOp",EDGE,"E130"),sQuery(id+"F0.wireOp",EDGE,"E131"),sQuery(id+"F0.wireOp",EDGE,"E132"),sQuery(id+"F0.wireOp",EDGE,"E133"),sQuery(id+"F0.wireOp",EDGE,"E134"),sQuery(id+"F0.wireOp",EDGE,"E135"),sQuery(id+"F0.wireOp",EDGE,"E136"),sQuery(id+"F0.wireOp",EDGE,"E137"),sQuery(id+"F0.wireOp",EDGE,"E138"),sQuery(id+"F0.wireOp",EDGE,"E139"),sQuery(id+"F0.wireOp",EDGE,"E140"),sQuery(id+"F0.wireOp",EDGE,"E141"),sQuery(id+"F0.wireOp",EDGE,"E142"),sQuery(id+"F0.wireOp",EDGE,"E143"),sQuery(id+"F0.wireOp",EDGE,"E144"),sQuery(id+"F0.wireOp",EDGE,"E145"),sQuery(id+"F0.wireOp",EDGE,"E146"),sQuery(id+"F0.wireOp",EDGE,"E147"),sQuery(id+"F0.wireOp",EDGE,"E148"),sQuery(id+"F0.wireOp",EDGE,"E149"),sQuery(id+"F0.wireOp",EDGE,"E150"),sQuery(id+"F0.wireOp",EDGE,"E151"),sQuery(id+"F0.wireOp",EDGE,"E152"),sQuery(id+"F0.wireOp",EDGE,"E153"),sQuery(id+"F0.wireOp",EDGE,"E154"),sQuery(id+"F0.wireOp",EDGE,"E155"),sQuery(id+"F0.wireOp",EDGE,"E156"),sQuery(id+"F0.wireOp",EDGE,"E157"),sQuery(id+"F0.wireOp",EDGE,"E158"),sQuery(id+"F0.wireOp",EDGE,"E159"),sQuery(id+"F0.wireOp",EDGE,"E160"),sQuery(id+"F0.wireOp",EDGE,"E161"),sQuery(id+"F0.wireOp",EDGE,"E162"),sQuery(id+"F0.wireOp",EDGE,"E163"),sQuery(id+"F0.wireOp",EDGE,"E164"),sQuery(id+"F0.wireOp",EDGE,"E165"),sQuery(id+"F0.wireOp",EDGE,"E166"),sQuery(id+"F0.wireOp",EDGE,"E167"),sQuery(id+"F0.wireOp",EDGE,"E168"),sQuery(id+"F0.wireOp",EDGE,"E169"),sQuery(id+"F0.wireOp",EDGE,"E170"),sQuery(id+"F0.wireOp",EDGE,"E171"),sQuery(id+"F0.wireOp",EDGE,"E172"),sQuery(id+"F0.wireOp",EDGE,"E173"),sQuery(id+"F0.wireOp",EDGE,"E174"),sQuery(id+"F0.wireOp",EDGE,"E175"),sQuery(id+"F0.wireOp",EDGE,"E176"),sQuery(id+"F0.wireOp",EDGE,"E177"),sQuery(id+"F0.wireOp",EDGE,"E178"),sQuery(id+"F0.wireOp",EDGE,"E179"),sQuery(id+"F0.wireOp",EDGE,"E180"),sQuery(id+"F0.wireOp",EDGE,"E181"),sQuery(id+"F0.wireOp",EDGE,"E182"),sQuery(id+"F0.wireOp",EDGE,"E183"),sQuery(id+"F0.wireOp",EDGE,"E184"),sQuery(id+"F0.wireOp",EDGE,"E185"),sQuery(id+"F0.wireOp",EDGE,"E186"),sQuery(id+"F0.wireOp",EDGE,"E187"),sQuery(id+"F0.wireOp",EDGE,"E188"),sQuery(id+"F0.wireOp",EDGE,"E189"),sQuery(id+"F0.wireOp",EDGE,"E190"),sQuery(id+"F0.wireOp",EDGE,"E191"),sQuery(id+"F0.wireOp",EDGE,"E192"),sQuery(id+"F0.wireOp",EDGE,"E193"),sQuery(id+"F0.wireOp",EDGE,"E194"),sQuery(id+"F0.wireOp",EDGE,"E195"),sQuery(id+"F0.wireOp",EDGE,"E196"),sQuery(id+"F0.wireOp",EDGE,"E197"),sQuery(id+"F0.wireOp",EDGE,"E198"),sQuery(id+"F0.wireOp",EDGE,"E199"),sQuery(id+"F0.wireOp",EDGE,"E200"),sQuery(id+"F0.wireOp",EDGE,"E201"),sQuery(id+"F0.wireOp",EDGE,"E202"),sQuery(id+"F0.wireOp",EDGE,"E203"),sQuery(id+"F0.wireOp",EDGE,"E204"),sQuery(id+"F0.wireOp",EDGE,"E205"),sQuery(id+"F0.wireOp",EDGE,"E206"),sQuery(id+"F0.wireOp",EDGE,"E207"),sQuery(id+"F0.wireOp",EDGE,"E208"),sQuery(id+"F0.wireOp",EDGE,"E209"),sQuery(id+"F0.wireOp",EDGE,"E210"),sQuery(id+"F0.wireOp",EDGE,"E211"),sQuery(id+"F0.wireOp",EDGE,"E212"),sQuery(id+"F0.wireOp",EDGE,"E213"),sQuery(id+"F0.wireOp",EDGE,"E214"),sQuery(id+"F0.wireOp",EDGE,"E215"),sQuery(id+"F0.wireOp",EDGE,"E216"),sQuery(id+"F0.wireOp",EDGE,"E217"),sQuery(id+"F0.wireOp",EDGE,"E218"),sQuery(id+"F0.wireOp",EDGE,"E219"),sQuery(id+"F0.wireOp",EDGE,"E220"),sQuery(id+"F0.wireOp",EDGE,"E221"),sQuery(id+"F0.wireOp",EDGE,"E222"),sQuery(id+"F0.wireOp",EDGE,"E223"),sQuery(id+"F0.wireOp",EDGE,"E224"),sQuery(id+"F0.wireOp",EDGE,"E225"),sQuery(id+"F0.wireOp",EDGE,"E226"),sQuery(id+"F0.wireOp",EDGE,"E227"),sQuery(id+"F0.wireOp",EDGE,"E228"),sQuery(id+"F0.wireOp",EDGE,"E229"),sQuery(id+"F0.wireOp",EDGE,"E230"),sQuery(id+"F0.wireOp",EDGE,"E231"),sQuery(id+"F0.wireOp",EDGE,"E232"),sQuery(id+"F0.wireOp",EDGE,"E233")])],"isStart":false});
            var sketch = newSketch(context, id + "F2", { "sketchPlane" : qUnion([Q0])});
            skLineSegment(sketch, "E236", {"start": v(-720.8, -813.23) * mm, "end": v(-720.8, -768.23) * mm, "construction": true});
            skLineSegment(sketch, "E237", {"start": v(-675.04, -553.46) * mm, "end": v(-675.04, -768.23) * mm, "construction": true});
            skLineSegment(sketch, "E238", {"start": v(-461.04, -553.46) * mm, "end": v(-461.04, -768.23) * mm, "construction": true});
            skLineSegment(sketch, "E239.bottom", {"start": v(-675.04, -768.23) * mm, "end": v(-461.04, -768.23) * mm});
            skLineSegment(sketch, "E239.top", {"start": v(-675.04, -711.23) * mm, "end": v(-461.04, -711.23) * mm});
            skLineSegment(sketch, "E239.left", {"start": v(-675.04, -768.23) * mm, "end": v(-675.04, -711.23) * mm});
            skLineSegment(sketch, "E239.right", {"start": v(-461.04, -768.23) * mm, "end": v(-461.04, -711.23) * mm});
            skLineSegment(sketch, "E240.top", {"start": v(-675.04, -673.23) * mm, "end": v(-461.04, -673.23) * mm});
            skLineSegment(sketch, "E240.left", {"start": v(-675.04, -711.23) * mm, "end": v(-675.04, -673.23) * mm});
            skLineSegment(sketch, "E240.right", {"start": v(-461.04, -711.23) * mm, "end": v(-461.04, -673.23) * mm});
            skLineSegment(sketch, "E241.left", {"start": v(-675.04, -673.23) * mm, "end": v(-675.04, -711.23) * mm});
            skLineSegment(sketch, "E241.right", {"start": v(-461.04, -673.23) * mm, "end": v(-461.04, -711.23) * mm});
            skLineSegment(sketch, "E242.bottom", {"start": v(-675.04, -730.23) * mm, "end": v(-461.04, -730.23) * mm});
            skLineSegment(sketch, "E242.left", {"start": v(-675.04, -730.23) * mm, "end": v(-675.04, -711.23) * mm});
            skLineSegment(sketch, "E242.right", {"start": v(-461.04, -730.23) * mm, "end": v(-461.04, -711.23) * mm});
            skLineSegment(sketch, "E243.left", {"start": v(-675.04, -768.23) * mm, "end": v(-675.04, -730.23) * mm});
            skLineSegment(sketch, "E243.right", {"start": v(-461.04, -768.23) * mm, "end": v(-461.04, -730.23) * mm});
            skSolve(sketch);
        }
        {
            var Q0;
            Q0=makeQuery(id+"F1.opExtrude","CAP_FACE",FACE,{"disambiguationData":[OSD([sQuery(id+"F0.wireOp",EDGE,"E0"),sQuery(id+"F0.wireOp",EDGE,"E1"),sQuery(id+"F0.wireOp",EDGE,"E2"),sQuery(id+"F0.wireOp",EDGE,"E3"),sQuery(id+"F0.wireOp",EDGE,"E4"),sQuery(id+"F0.wireOp",EDGE,"E5"),sQuery(id+"F0.wireOp",EDGE,"E6"),sQuery(id+"F0.wireOp",EDGE,"E7"),sQuery(id+"F0.wireOp",EDGE,"E8"),sQuery(id+"F0.wireOp",EDGE,"E9"),sQuery(id+"F0.wireOp",EDGE,"E10"),sQuery(id+"F0.wireOp",EDGE,"E11"),sQuery(id+"F0.wireOp",EDGE,"E12"),sQuery(id+"F0.wireOp",EDGE,"E13"),sQuery(id+"F0.wireOp",EDGE,"E14"),sQuery(id+"F0.wireOp",EDGE,"E15"),sQuery(id+"F0.wireOp",EDGE,"E16"),sQuery(id+"F0.wireOp",EDGE,"E17"),sQuery(id+"F0.wireOp",EDGE,"E18"),sQuery(id+"F0.wireOp",EDGE,"E19"),sQuery(id+"F0.wireOp",EDGE,"E20"),sQuery(id+"F0.wireOp",EDGE,"E21"),sQuery(id+"F0.wireOp",EDGE,"E22"),sQuery(id+"F0.wireOp",EDGE,"E23"),sQuery(id+"F0.wireOp",EDGE,"E24"),sQuery(id+"F0.wireOp",EDGE,"E25"),sQuery(id+"F0.wireOp",EDGE,"E26"),sQuery(id+"F0.wireOp",EDGE,"E27"),sQuery(id+"F0.wireOp",EDGE,"E28"),sQuery(id+"F0.wireOp",EDGE,"E29"),sQuery(id+"F0.wireOp",EDGE,"E30"),sQuery(id+"F0.wireOp",EDGE,"E31"),sQuery(id+"F0.wireOp",EDGE,"E32"),sQuery(id+"F0.wireOp",EDGE,"E33"),sQuery(id+"F0.wireOp",EDGE,"E34"),sQuery(id+"F0.wireOp",EDGE,"E35"),sQuery(id+"F0.wireOp",EDGE,"E36"),sQuery(id+"F0.wireOp",EDGE,"E37"),sQuery(id+"F0.wireOp",EDGE,"E38"),sQuery(id+"F0.wireOp",EDGE,"E39"),sQuery(id+"F0.wireOp",EDGE,"E40"),sQuery(id+"F0.wireOp",EDGE,"E41"),sQuery(id+"F0.wireOp",EDGE,"E42"),sQuery(id+"F0.wireOp",EDGE,"E43"),sQuery(id+"F0.wireOp",EDGE,"E44"),sQuery(id+"F0.wireOp",EDGE,"E45"),sQuery(id+"F0.wireOp",EDGE,"E46"),sQuery(id+"F0.wireOp",EDGE,"E47"),sQuery(id+"F0.wireOp",EDGE,"E48"),sQuery(id+"F0.wireOp",EDGE,"E49"),sQuery(id+"F0.wireOp",EDGE,"E50"),sQuery(id+"F0.wireOp",EDGE,"E51"),sQuery(id+"F0.wireOp",EDGE,"E52"),sQuery(id+"F0.wireOp",EDGE,"E53"),sQuery(id+"F0.wireOp",EDGE,"E54"),sQuery(id+"F0.wireOp",EDGE,"E55"),sQuery(id+"F0.wireOp",EDGE,"E56"),sQuery(id+"F0.wireOp",EDGE,"E57"),sQuery(id+"F0.wireOp",EDGE,"E58"),sQuery(id+"F0.wireOp",EDGE,"E59"),sQuery(id+"F0.wireOp",EDGE,"E60"),sQuery(id+"F0.wireOp",EDGE,"E61"),sQuery(id+"F0.wireOp",EDGE,"E62"),sQuery(id+"F0.wireOp",EDGE,"E63"),sQuery(id+"F0.wireOp",EDGE,"E64"),sQuery(id+"F0.wireOp",EDGE,"E65"),sQuery(id+"F0.wireOp",EDGE,"E66"),sQuery(id+"F0.wireOp",EDGE,"E67"),sQuery(id+"F0.wireOp",EDGE,"E68"),sQuery(id+"F0.wireOp",EDGE,"E69"),sQuery(id+"F0.wireOp",EDGE,"E70"),sQuery(id+"F0.wireOp",EDGE,"E71"),sQuery(id+"F0.wireOp",EDGE,"E72"),sQuery(id+"F0.wireOp",EDGE,"E73"),sQuery(id+"F0.wireOp",EDGE,"E74"),sQuery(id+"F0.wireOp",EDGE,"E75"),sQuery(id+"F0.wireOp",EDGE,"E76"),sQuery(id+"F0.wireOp",EDGE,"E77"),sQuery(id+"F0.wireOp",EDGE,"E78"),sQuery(id+"F0.wireOp",EDGE,"E79"),sQuery(id+"F0.wireOp",EDGE,"E80"),sQuery(id+"F0.wireOp",EDGE,"E81"),sQuery(id+"F0.wireOp",EDGE,"E82"),sQuery(id+"F0.wireOp",EDGE,"E83"),sQuery(id+"F0.wireOp",EDGE,"E84"),sQuery(id+"F0.wireOp",EDGE,"E85"),sQuery(id+"F0.wireOp",EDGE,"E86"),sQuery(id+"F0.wireOp",EDGE,"E87"),sQuery(id+"F0.wireOp",EDGE,"E88"),sQuery(id+"F0.wireOp",EDGE,"E89"),sQuery(id+"F0.wireOp",EDGE,"E90"),sQuery(id+"F0.wireOp",EDGE,"E91"),sQuery(id+"F0.wireOp",EDGE,"E92"),sQuery(id+"F0.wireOp",EDGE,"E93"),sQuery(id+"F0.wireOp",EDGE,"E94"),sQuery(id+"F0.wireOp",EDGE,"E95"),sQuery(id+"F0.wireOp",EDGE,"E96"),sQuery(id+"F0.wireOp",EDGE,"E97"),sQuery(id+"F0.wireOp",EDGE,"E98"),sQuery(id+"F0.wireOp",EDGE,"E99"),sQuery(id+"F0.wireOp",EDGE,"E100"),sQuery(id+"F0.wireOp",EDGE,"E101"),sQuery(id+"F0.wireOp",EDGE,"E102"),sQuery(id+"F0.wireOp",EDGE,"E103"),sQuery(id+"F0.wireOp",EDGE,"E104"),sQuery(id+"F0.wireOp",EDGE,"E105"),sQuery(id+"F0.wireOp",EDGE,"E106"),sQuery(id+"F0.wireOp",EDGE,"E107"),sQuery(id+"F0.wireOp",EDGE,"E108"),sQuery(id+"F0.wireOp",EDGE,"E109"),sQuery(id+"F0.wireOp",EDGE,"E110"),sQuery(id+"F0.wireOp",EDGE,"E111"),sQuery(id+"F0.wireOp",EDGE,"E112"),sQuery(id+"F0.wireOp",EDGE,"E113"),sQuery(id+"F0.wireOp",EDGE,"E114"),sQuery(id+"F0.wireOp",EDGE,"E115"),sQuery(id+"F0.wireOp",EDGE,"E116"),sQuery(id+"F0.wireOp",EDGE,"E117"),sQuery(id+"F0.wireOp",EDGE,"E118"),sQuery(id+"F0.wireOp",EDGE,"E119"),sQuery(id+"F0.wireOp",EDGE,"E120"),sQuery(id+"F0.wireOp",EDGE,"E121"),sQuery(id+"F0.wireOp",EDGE,"E122"),sQuery(id+"F0.wireOp",EDGE,"E123"),sQuery(id+"F0.wireOp",EDGE,"E124"),sQuery(id+"F0.wireOp",EDGE,"E125"),sQuery(id+"F0.wireOp",EDGE,"E126"),sQuery(id+"F0.wireOp",EDGE,"E127"),sQuery(id+"F0.wireOp",EDGE,"E128"),sQuery(id+"F0.wireOp",EDGE,"E129"),sQuery(id+"F0.wireOp",EDGE,"E130"),sQuery(id+"F0.wireOp",EDGE,"E131"),sQuery(id+"F0.wireOp",EDGE,"E132"),sQuery(id+"F0.wireOp",EDGE,"E133"),sQuery(id+"F0.wireOp",EDGE,"E134"),sQuery(id+"F0.wireOp",EDGE,"E135"),sQuery(id+"F0.wireOp",EDGE,"E136"),sQuery(id+"F0.wireOp",EDGE,"E137"),sQuery(id+"F0.wireOp",EDGE,"E138"),sQuery(id+"F0.wireOp",EDGE,"E139"),sQuery(id+"F0.wireOp",EDGE,"E140"),sQuery(id+"F0.wireOp",EDGE,"E141"),sQuery(id+"F0.wireOp",EDGE,"E142"),sQuery(id+"F0.wireOp",EDGE,"E143"),sQuery(id+"F0.wireOp",EDGE,"E144"),sQuery(id+"F0.wireOp",EDGE,"E145"),sQuery(id+"F0.wireOp",EDGE,"E146"),sQuery(id+"F0.wireOp",EDGE,"E147"),sQuery(id+"F0.wireOp",EDGE,"E148"),sQuery(id+"F0.wireOp",EDGE,"E149"),sQuery(id+"F0.wireOp",EDGE,"E150"),sQuery(id+"F0.wireOp",EDGE,"E151"),sQuery(id+"F0.wireOp",EDGE,"E152"),sQuery(id+"F0.wireOp",EDGE,"E153"),sQuery(id+"F0.wireOp",EDGE,"E154"),sQuery(id+"F0.wireOp",EDGE,"E155"),sQuery(id+"F0.wireOp",EDGE,"E156"),sQuery(id+"F0.wireOp",EDGE,"E157"),sQuery(id+"F0.wireOp",EDGE,"E158"),sQuery(id+"F0.wireOp",EDGE,"E159"),sQuery(id+"F0.wireOp",EDGE,"E160"),sQuery(id+"F0.wireOp",EDGE,"E161"),sQuery(id+"F0.wireOp",EDGE,"E162"),sQuery(id+"F0.wireOp",EDGE,"E163"),sQuery(id+"F0.wireOp",EDGE,"E164"),sQuery(id+"F0.wireOp",EDGE,"E165"),sQuery(id+"F0.wireOp",EDGE,"E166"),sQuery(id+"F0.wireOp",EDGE,"E167"),sQuery(id+"F0.wireOp",EDGE,"E168"),sQuery(id+"F0.wireOp",EDGE,"E169"),sQuery(id+"F0.wireOp",EDGE,"E170"),sQuery(id+"F0.wireOp",EDGE,"E171"),sQuery(id+"F0.wireOp",EDGE,"E172"),sQuery(id+"F0.wireOp",EDGE,"E173"),sQuery(id+"F0.wireOp",EDGE,"E174"),sQuery(id+"F0.wireOp",EDGE,"E175"),sQuery(id+"F0.wireOp",EDGE,"E176"),sQuery(id+"F0.wireOp",EDGE,"E177"),sQuery(id+"F0.wireOp",EDGE,"E178"),sQuery(id+"F0.wireOp",EDGE,"E179"),sQuery(id+"F0.wireOp",EDGE,"E180"),sQuery(id+"F0.wireOp",EDGE,"E181"),sQuery(id+"F0.wireOp",EDGE,"E182"),sQuery(id+"F0.wireOp",EDGE,"E183"),sQuery(id+"F0.wireOp",EDGE,"E184"),sQuery(id+"F0.wireOp",EDGE,"E185"),sQuery(id+"F0.wireOp",EDGE,"E186"),sQuery(id+"F0.wireOp",EDGE,"E187"),sQuery(id+"F0.wireOp",EDGE,"E188"),sQuery(id+"F0.wireOp",EDGE,"E189"),sQuery(id+"F0.wireOp",EDGE,"E190"),sQuery(id+"F0.wireOp",EDGE,"E191"),sQuery(id+"F0.wireOp",EDGE,"E192"),sQuery(id+"F0.wireOp",EDGE,"E193"),sQuery(id+"F0.wireOp",EDGE,"E194"),sQuery(id+"F0.wireOp",EDGE,"E195"),sQuery(id+"F0.wireOp",EDGE,"E196"),sQuery(id+"F0.wireOp",EDGE,"E197"),sQuery(id+"F0.wireOp",EDGE,"E198"),sQuery(id+"F0.wireOp",EDGE,"E199"),sQuery(id+"F0.wireOp",EDGE,"E200"),sQuery(id+"F0.wireOp",EDGE,"E201"),sQuery(id+"F0.wireOp",EDGE,"E210"),sQuery(id+"F0.wireOp",EDGE,"E211"),sQuery(id+"F0.wireOp",EDGE,"E212"),sQuery(id+"F0.wireOp",EDGE,"E213"),sQuery(id+"F0.wireOp",EDGE,"E214"),sQuery(id+"F0.wireOp",EDGE,"E215"),sQuery(id+"F0.wireOp",EDGE,"E216"),sQuery(id+"F0.wireOp",EDGE,"E217"),sQuery(id+"F0.wireOp",EDGE,"E218"),sQuery(id+"F0.wireOp",EDGE,"E219"),sQuery(id+"F0.wireOp",EDGE,"E220"),sQuery(id+"F0.wireOp",EDGE,"E221"),sQuery(id+"F0.wireOp",EDGE,"E222"),sQuery(id+"F0.wireOp",EDGE,"E223"),sQuery(id+"F0.wireOp",EDGE,"E224"),sQuery(id+"F0.wireOp",EDGE,"E225"),sQuery(id+"F0.wireOp",EDGE,"E226"),sQuery(id+"F0.wireOp",EDGE,"E227"),sQuery(id+"F0.wireOp",EDGE,"E228"),sQuery(id+"F0.wireOp",EDGE,"E229"),sQuery(id+"F0.wireOp",EDGE,"E230"),sQuery(id+"F0.wireOp",EDGE,"E231"),sQuery(id+"F0.wireOp",EDGE,"E232"),sQuery(id+"F0.wireOp",EDGE,"E233")])],"isStart":false});
            var sketch = newSketch(context, id + "F3", { "sketchPlane" : qUnion([Q0])});
            skLineSegment(sketch, "E244", {"start": v(-568.04, -780.98) * mm, "end": v(-640.54, -780.98) * mm});
            skLineSegment(sketch, "E245", {"start": v(-640.54, -780.98) * mm, "end": v(-640.54, -826.98) * mm});
            skLineSegment(sketch, "E246", {"start": v(-568.04, -780.98) * mm, "end": v(-568.04, -860.85) * mm, "construction": true});
            skLineSegment(sketch, "E247", {"start": v(-640.54, -826.98) * mm, "end": v(-568.04, -826.98) * mm});
            skLineSegment(sketch, "E248.top", {"start": v(-640.54, -871.98) * mm, "end": v(-568.04, -871.98) * mm});
            skLineSegment(sketch, "E248.left", {"start": v(-640.54, -826.98) * mm, "end": v(-640.54, -871.98) * mm});
            skLineSegment(sketch, "E248.right", {"start": v(-568.04, -826.98) * mm, "end": v(-568.04, -871.98) * mm});
            skLineSegment(sketch, "E249.MirrorCS", {"start": v(-495.54, -826.98) * mm, "end": v(-568.04, -826.98) * mm});
            skLineSegment(sketch, "E250.MirrorCS", {"start": v(-568.04, -780.98) * mm, "end": v(-495.54, -780.98) * mm});
            skLineSegment(sketch, "E251.MirrorCS", {"start": v(-495.54, -780.98) * mm, "end": v(-495.54, -826.98) * mm});
            skLineSegment(sketch, "E252.MirrorCS", {"start": v(-495.54, -826.98) * mm, "end": v(-495.54, -871.98) * mm});
            skLineSegment(sketch, "E253.MirrorCS", {"start": v(-495.54, -871.98) * mm, "end": v(-568.04, -871.98) * mm});
            skLineSegment(sketch, "E254.bottom", {"start": v(-640.54, -780.98) * mm, "end": v(-495.54, -780.98) * mm});
            skLineSegment(sketch, "E254.top", {"start": v(-640.54, -781.98) * mm, "end": v(-495.54, -781.98) * mm});
            skLineSegment(sketch, "E254.left", {"start": v(-640.54, -780.98) * mm, "end": v(-640.54, -781.98) * mm});
            skLineSegment(sketch, "E254.right", {"start": v(-495.54, -780.98) * mm, "end": v(-495.54, -781.98) * mm});
            skLineSegment(sketch, "E255.bottom", {"start": v(-568.04, -871.98) * mm, "end": v(-636.83, -871.98) * mm});
            skLineSegment(sketch, "E255.top", {"start": v(-568.04, -882.58) * mm, "end": v(-636.83, -882.58) * mm});
            skLineSegment(sketch, "E255.left", {"start": v(-568.04, -871.98) * mm, "end": v(-568.04, -882.58) * mm});
            skLineSegment(sketch, "E255.right", {"start": v(-636.83, -871.98) * mm, "end": v(-636.83, -882.58) * mm});
            skLineSegment(sketch, "E256", {"start": v(-636.83, -872.98) * mm, "end": v(-568.04, -872.98) * mm});
            skLineSegment(sketch, "E257.bottom", {"start": v(-636.83, -1070.18) * mm, "end": v(-568.04, -1070.18) * mm});
            skLineSegment(sketch, "E257.top", {"start": v(-636.83, -1079.78) * mm, "end": v(-568.04, -1079.78) * mm});
            skLineSegment(sketch, "E257.left", {"start": v(-636.83, -1070.18) * mm, "end": v(-636.83, -1079.78) * mm});
            skLineSegment(sketch, "E257.right", {"start": v(-568.04, -1070.18) * mm, "end": v(-568.04, -1079.78) * mm});
            skLineSegment(sketch, "E258.bottom", {"start": v(-568.04, -882.58) * mm, "end": v(-571.19, -882.58) * mm});
            skLineSegment(sketch, "E258.top", {"start": v(-568.04, -1070.18) * mm, "end": v(-571.19, -1070.18) * mm});
            skLineSegment(sketch, "E258.left", {"start": v(-568.04, -882.58) * mm, "end": v(-568.04, -1070.18) * mm});
            skLineSegment(sketch, "E258.right", {"start": v(-571.19, -882.58) * mm, "end": v(-571.19, -1070.18) * mm});
            skLineSegment(sketch, "E259.MirrorCS", {"start": v(-499.24, -871.98) * mm, "end": v(-499.24, -882.58) * mm});
            skLineSegment(sketch, "E260.MirrorCS", {"start": v(-499.24, -872.98) * mm, "end": v(-568.04, -872.98) * mm});
            skLineSegment(sketch, "E261.MirrorCS", {"start": v(-568.04, -882.58) * mm, "end": v(-499.24, -882.58) * mm});
            skLineSegment(sketch, "E262.MirrorCS", {"start": v(-568.04, -1070.18) * mm, "end": v(-564.89, -1070.18) * mm});
            skLineSegment(sketch, "E263.MirrorCS", {"start": v(-499.24, -1070.18) * mm, "end": v(-499.24, -1079.78) * mm});
            skLineSegment(sketch, "E264.MirrorCS", {"start": v(-564.89, -882.58) * mm, "end": v(-564.89, -1070.18) * mm});
            skLineSegment(sketch, "E265.MirrorCS", {"start": v(-499.24, -1079.78) * mm, "end": v(-568.04, -1079.78) * mm});
            skLineSegment(sketch, "E266.MirrorCS", {"start": v(-499.24, -1070.18) * mm, "end": v(-568.04, -1070.18) * mm});
            skSolve(sketch);
        }
        {
            var Q0;
            Q0=makeQuery(id+"F3.imprint","IMPRINT",FACE,{"disambiguationData":[TD([[makeQuery(id+"F3.imprint","IMPRINT",EDGE,{"derivedFrom":sQuery(id+"F3.wireOp",EDGE,"E245")}),1.0]])]});
            extrude(context, id + "F4", {"entities" : qUnion([Q0]), "endBound" : BoundingType.SYMMETRIC, "depth" : 300 * mm});
        }
        {
            var Q0;
            Q0=makeQuery(id+"F3.imprint","IMPRINT",FACE,{"disambiguationData":[TD([[makeQuery(id+"F3.imprint","IMPRINT",EDGE,{"derivedFrom":sQuery(id+"F3.wireOp",EDGE,"E247")}),-1.0]])]});
            var Q1;
            Q1=makeQuery(id+"F3.imprint","IMPRINT",FACE,{"disambiguationData":[TD([[makeQuery(id+"F3.imprint","IMPRINT",EDGE,{"derivedFrom":sQuery(id+"F3.wireOp",EDGE,"E248.right")}),1.0]])]});
            extrude(context, id + "F5", {"entities" : qUnion([Q0, Q1]), "endBound" : BoundingType.SYMMETRIC, "depth" : 300 * mm});
        }
        {
            var Q0;
            Q0=makeQuery(id+"F5.opExtrude","SWEPT_FACE",FACE,{"disambiguationData":[OSD([sQuery(id+"F3.wireOp",EDGE,"E248.top"),sQuery(id+"F3.wireOp",EDGE,"E253.MirrorCS")])]});
            var sketch = newSketch(context, id + "F6", { "sketchPlane" : qUnion([Q0])});
            skLineSegment(sketch, "E267", {"start": v(-640.54, 75) * mm, "end": v(-495.54, 75) * mm, "construction": true});
            skLineSegment(sketch, "E268", {"start": v(-640.54, 18) * mm, "end": v(-495.54, 18) * mm, "construction": true});
            skLineSegment(sketch, "E269", {"start": v(-568.04, 75) * mm, "end": v(-568.04, 99.7) * mm, "construction": true});
            skLineSegment(sketch, "E270", {"start": v(-608.04, 75) * mm, "end": v(-608.04, 75) * mm});
            skLineSegment(sketch, "E271", {"start": v(-528.04, 75) * mm, "end": v(-528.04, 75) * mm});
            skCircle(sketch, "E272", {"center": v(-608.04, 75) * mm, "radius": 8 * mm});
            skCircle(sketch, "E273", {"center": v(-528.04, 75) * mm, "radius": 8 * mm});
            skSolve(sketch);
        }
        {
            var Q0;
            {var subQ4=sQuery(id+"F3.wireOp",EDGE,"E260.MirrorCS");Q0=makeQuery(id+"F3.imprint","IMPRINT",FACE,{"disambiguationData":[TD([[makeQuery(id+"F3.imprint","IMPRINT",EDGE,{"derivedFrom":subQ4}),1.0]])]});}
            var Q1;
            {var subQ1=sQuery(id+"F3.wireOp",EDGE,"E255.top");Q1=makeQuery(id+"F3.imprint","IMPRINT",FACE,{"disambiguationData":[TD([[makeQuery(id+"F3.imprint","IMPRINT",EDGE,{"derivedFrom":subQ1}),-1.0]])]});}
            var Q2;
            {var subQ0=sQuery(id+"F3.wireOp",EDGE,"E258.left");Q2=makeQuery(id+"F3.imprint","IMPRINT",FACE,{"disambiguationData":[TD([[makeQuery(id+"F3.imprint","IMPRINT",EDGE,{"derivedFrom":subQ0}),1.0]])]});}
            var Q3;
            Q3=makeQuery(id+"F3.imprint","IMPRINT",FACE,{"disambiguationData":[TD([[makeQuery(id+"F3.imprint","IMPRINT",EDGE,{"derivedFrom":sQuery(id+"F3.wireOp",EDGE,"E258.bottom")}),1.0]])]});
            var Q4;
            {var subQ1=sQuery(id+"F3.wireOp",EDGE,"E257.right");Q4=makeQuery(id+"F3.imprint","IMPRINT",FACE,{"disambiguationData":[TD([[makeQuery(id+"F3.imprint","IMPRINT",EDGE,{"derivedFrom":subQ1}),1.0]])]});}
            var Q5;
            Q5=makeQuery(id+"F3.imprint","IMPRINT",FACE,{"disambiguationData":[TD([[makeQuery(id+"F3.imprint","IMPRINT",EDGE,{"derivedFrom":sQuery(id+"F3.wireOp",EDGE,"E257.bottom")}),-1.0]])]});
            extrude(context, id + "F7", {"entities" : qUnion([Q0, Q1, Q2, Q3, Q4, Q5]), "endBound" : BoundingType.SYMMETRIC, "depth" : 300 * mm});
        }
        {
            var Q0;
            Q0=makeQuery(id+"F6.imprint","IMPRINT",FACE,{"disambiguationData":[TD([[makeQuery(id+"F6.imprint","IMPRINT",EDGE,{"derivedFrom":sQuery(id+"F6.wireOp",EDGE,"E272")}),1.0]])]});
            var Q1;
            Q1=makeQuery(id+"F6.imprint","IMPRINT",FACE,{"disambiguationData":[TD([[makeQuery(id+"F6.imprint","IMPRINT",EDGE,{"derivedFrom":sQuery(id+"F6.wireOp",EDGE,"E273")}),1.0]])]});
            extrude(context, id + "F8", {"entities" : qUnion([Q0, Q1]), "operationType" : NewBodyOperationType.REMOVE, "endBound" : BoundingType.SYMMETRIC, "oppositeDirection" : true, "depth" : 200 * mm});
        }
        {
            var Q0;
            Q0=makeQuery(id+"F2.imprint","IMPRINT",FACE,{"disambiguationData":[TD([[makeQuery(id+"F2.imprint","IMPRINT",EDGE,{"derivedFrom":sQuery(id+"F2.wireOp",EDGE,"E240.top")}),-1.0]])]});
            var Q1;
            Q1=makeQuery(id+"F2.imprint","IMPRINT",FACE,{"disambiguationData":[TD([[makeQuery(id+"F2.imprint","IMPRINT",EDGE,{"derivedFrom":sQuery(id+"F2.wireOp",EDGE,"E239.bottom")}),1.0]])]});
            extrude(context, id + "F9", {"entities" : qUnion([Q0, Q1]), "depth" : 114 * mm});
        }
        {
            var Q0;
            Q0=makeQuery(id+"F9.opExtrude","SWEPT_FACE",FACE,{"disambiguationData":[OSD([sQuery(id+"F2.wireOp",EDGE,"E240.top")])]});
            var sketch = newSketch(context, id + "F10", { "sketchPlane" : qUnion([Q0])});
            skLineSegment(sketch, "E274", {"start": v(-568.04, -18) * mm, "end": v(-568.04, -132) * mm, "construction": true});
            skPoint(sketch, "E275", {"position": v(-568.04, -75) * mm});
            skLineSegment(sketch, "E276.bottom", {"start": v(-528.04, -92.25) * mm, "end": v(-608.04, -92.25) * mm, "construction": true});
            skLineSegment(sketch, "E276.top", {"start": v(-528.04, -57.75) * mm, "end": v(-608.04, -57.75) * mm, "construction": true});
            skLineSegment(sketch, "E276.left", {"start": v(-528.04, -92.25) * mm, "end": v(-528.04, -57.75) * mm, "construction": true});
            skLineSegment(sketch, "E276.right", {"start": v(-608.04, -92.25) * mm, "end": v(-608.04, -57.75) * mm, "construction": true});
            skCircle(sketch, "E277", {"center": v(-608.04, -75) * mm, "radius": 12.5 * mm});
            skCircle(sketch, "E278", {"center": v(-528.04, -75) * mm, "radius": 12.5 * mm});
            skLineSegment(sketch, "E279.bottom", {"start": v(-478.04, -115) * mm, "end": v(-658.04, -115) * mm});
            skLineSegment(sketch, "E279.top", {"start": v(-478.04, -35) * mm, "end": v(-658.04, -35) * mm});
            skLineSegment(sketch, "E279.left", {"start": v(-478.04, -115) * mm, "end": v(-478.04, -35) * mm});
            skLineSegment(sketch, "E279.right", {"start": v(-658.04, -115) * mm, "end": v(-658.04, -35) * mm});
            skSolve(sketch);
        }
        {
            var Q0;
            Q0=makeQuery(id+"F10.imprint","IMPRINT",FACE,{"disambiguationData":[TD([[makeQuery(id+"F10.imprint","IMPRINT",EDGE,{"derivedFrom":sQuery(id+"F10.wireOp",EDGE,"E277")}),1.0]])]});
            var Q1;
            Q1=makeQuery(id+"F10.imprint","IMPRINT",FACE,{"disambiguationData":[TD([[makeQuery(id+"F10.imprint","IMPRINT",EDGE,{"derivedFrom":sQuery(id+"F10.wireOp",EDGE,"E278")}),1.0]])]});
            extrude(context, id + "F11", {"entities" : qUnion([Q0, Q1]), "operationType" : NewBodyOperationType.REMOVE, "depth" : -100 * mm});
        }
        {
            var Q0;
            Q0=makeQuery(id+"F10.imprint","IMPRINT",FACE,{"disambiguationData":[TD([[makeQuery(id+"F10.imprint","IMPRINT",EDGE,{"derivedFrom":sQuery(id+"F10.wireOp",EDGE,"E277")}),-1.0]])]});
            var Q1;
            Q1=makeQuery(id+"F10.imprint","IMPRINT",FACE,{"disambiguationData":[TD([[makeQuery(id+"F10.imprint","IMPRINT",EDGE,{"derivedFrom":sQuery(id+"F10.wireOp",EDGE,"E277")}),1.0]])]});
            var Q2;
            Q2=makeQuery(id+"F10.imprint","IMPRINT",FACE,{"disambiguationData":[TD([[makeQuery(id+"F10.imprint","IMPRINT",EDGE,{"derivedFrom":sQuery(id+"F10.wireOp",EDGE,"E278")}),1.0]])]});
            extrude(context, id + "F12", {"entities" : qUnion([Q0, Q1, Q2]), "depth" : 6 * mm});
        }
        {
            var Q0;
            Q0=makeQuery(id+"F12.opExtrude","CAP_FACE",FACE,{"disambiguationData":[OSD([sQuery(id+"F10.wireOp",EDGE,"E279.bottom"),sQuery(id+"F10.wireOp",EDGE,"E279.top"),sQuery(id+"F10.wireOp",EDGE,"E279.left"),sQuery(id+"F10.wireOp",EDGE,"E279.right")])],"isStart":false});
            var sketch = newSketch(context, id + "F13", { "sketchPlane" : qUnion([Q0])});
            skLineSegment(sketch, "E280", {"start": v(-568.04, -35) * mm, "end": v(-568.04, -115) * mm, "construction": true});
            skLineSegment(sketch, "E281.bottom", {"start": v(-528.04, -94.8) * mm, "end": v(-608.04, -94.8) * mm, "construction": true});
            skLineSegment(sketch, "E281.top", {"start": v(-528.04, -55.2) * mm, "end": v(-608.04, -55.2) * mm, "construction": true});
            skLineSegment(sketch, "E281.left", {"start": v(-528.04, -94.8) * mm, "end": v(-528.04, -55.2) * mm, "construction": true});
            skLineSegment(sketch, "E281.right", {"start": v(-608.04, -94.8) * mm, "end": v(-608.04, -55.2) * mm, "construction": true});
            skPoint(sketch, "E281.middle", {"position": v(-568.04, -75) * mm});
            skCircle(sketch, "E282", {"center": v(-608.04, -75) * mm, "radius": 7 * mm});
            skCircle(sketch, "E283", {"center": v(-528.04, -75) * mm, "radius": 7 * mm});
            skSolve(sketch);
        }
        {
            var Q0;
            Q0=makeQuery(id+"F13.imprint","IMPRINT",FACE,{"disambiguationData":[TD([[makeQuery(id+"F13.imprint","IMPRINT",EDGE,{"derivedFrom":sQuery(id+"F13.wireOp",EDGE,"E282")}),1.0]])]});
            var Q1;
            Q1=makeQuery(id+"F13.imprint","IMPRINT",FACE,{"disambiguationData":[TD([[makeQuery(id+"F13.imprint","IMPRINT",EDGE,{"derivedFrom":sQuery(id+"F13.wireOp",EDGE,"E283")}),1.0]])]});
            extrude(context, id + "F14", {"entities" : qUnion([Q0, Q1]), "operationType" : NewBodyOperationType.REMOVE, "oppositeDirection" : true, "depth" : 6 * mm});
        }
        {
            var Q0;
            Q0=makeQuery(id+"F2.imprint","IMPRINT",FACE,{"disambiguationData":[TD([[makeQuery(id+"F2.imprint","IMPRINT",EDGE,{"derivedFrom":sQuery(id+"F2.wireOp",EDGE,"E239.top")}),-1.0]])]});
            extrude(context, id + "F15", {"entities" : qUnion([Q0]), "depth" : 114 * mm});
        }
    });
